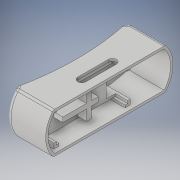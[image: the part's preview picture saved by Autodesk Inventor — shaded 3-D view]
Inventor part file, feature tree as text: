
AUTODESK INVENTOR PART (.ipt)
format: ipt  version: 2019 (Build 230136000, 136)  size: 523,264 bytes
history: native  units: in
note: dims shown in document units (in); Inventor stores cm internally (conversion verified against a paired STEP export)
features: extrude x11, sketch x11, projected_geometry x7, fillet x2, chamfer x1
ambient origin geometry x8: Origin, YZ Plane, XZ Plane, XY Plane, X Axis, Y Axis, Z Axis, Center Point
bodies: Solid1 (feature_tree)
feature tree (32):
  extrude  "Extrusion1"  Depth=1.5748in
  extrude  "Extrusion2"  Depth=0.2756in
  extrude  "Extrusion3"  Depth=2.7559in
  extrude  "Extrusion4"  Depth=0.1969in
  extrude  "Extrusion5"  Depth=0.1969in
  extrude  "Extrusion7"  Depth=0.1969in
  chamfer  "Chamfer1"  Distance=0.7874in
  extrude  "Extrusion8"  Depth=0.1181in TaperAngle=0.0deg
  extrude  "Extrusion9"  Depth=1.9685in TaperAngle=0.0deg
  extrude  "Extrusion10"  Depth=0.3543in TaperAngle=45.0deg
  extrude  "Extrusion11"  Depth=0.315in
  fillet  "Fillet3"  Radius=0.0945in
  fillet  "Fillet4"  Radius=1.4173in
  extrude  "Extrusion12"  Depth=0.315in TaperAngle=0.0deg
  sketch  "Sketch1"  dims[d0=4.3307in d1=1.5748in]
  sketch  "Sketch2"  dims[d2=0.0787in d3=0.0in d4=0.2756in]
  sketch  "Sketch3"  dims[d5=0.5906in d6=2.7559in]
  projected_geometry  "Projected Loop1"
  sketch  "Sketch4"  dims[d7=1.1811in d8=0.1969in]
  projected_geometry  "Projected Loop2"
  projected_geometry  "Projected Loop3"
  projected_geometry  "Projected Loop4"
  projected_geometry  "Projected Loop5"
  sketch  "Sketch5"  dims[d9=0.1969in d10=0.1969in]
  projected_geometry  "Projected Loop6"
  sketch  "Sketch7"  dims[d11=0.1969in d12=0.1969in]
  sketch  "Sketch9"  dims[d13=0.1969in d14=0.7874in d15=0.0in]
  sketch  "Sketch10"  dims[d16=0.3543in d17=0.0in d18=0.1181in d19=0.0in]
  sketch  "Sketch11"  dims[d20=0.0039in d21=1.9685in d22=0.0in]
  sketch  "Sketch12"  dims[d28=0.3543in d29=0.0in d31=0.3543in d32=0.0787in d33=45.0deg]
  projected_geometry  "Projected Loop7"
  sketch  "Sketch13"  dims[d34=1.1811in d35=1.1811in d36=0.0945in d37=1.4173in d38=0.0in d39=0.0787in d40=0.0in d41=1.7717in d42=0.0in d43=0.0984in d44=1.5748in d45=0.0in d46=0.1575in d47=0.1181in d49=0.4724in d50=0.5906in d51=0.315in d52=0.1181in d53=0.0in]
